# Revit family: 5863017284
name_source: partatom
category: Plumbing Fixtures
revit_build: Autodesk Revit 2018 (Build: 20170223_1515(x64)
units: mm (PartAtom-declared; Revit-internal decimal feet)

## family parameters
Always vertical = Yes
Cut with Voids When Loaded = No
OmniClass Number = 23.45.55.00
OmniClass Title = Sanitary Faucets, Wastes
Part Type = Normal
Room Calculation Point = No
Round Connector Dimension = Use Diameter
Shared = No
Work Plane-Based = No

## types (1)
- 5863017284 Shower faucet, 6 V, Bluetooth
    2D/3D/BIM Files URL = http://static.hansa.com
    3D View = https://static.hansa.com
    Additional Features = protected against back-flow in domestic use (according to DIN EN 1717)
    Advanced Features = Safety glass;Software settings adjustable via App
    Ambience photo = http://static.hansa.com
    AssetType = Fixed
    BIMObjectName = 5863017284
    Backflow Prevention EN1717 = EB
    Battery = AA 1.5 V Lithium x 4
    Bluetooth = 4.x
    BodyMaterial = Brass
    Brand = HANSA
    Catalog Drawing URL = http://static.hansa.com
    Category = Bathroom;Shower
    CloseOffRating = 0
    Color = 549
    Connection = Ball eccentric coupling(s)
    Connection Size = G1/2
    Dimension Drawing URL = http://static.hansa.com
    DurationUnit = Year
    EAN Number = 4057304008740
    EMC Directive = 2014/53/EU , 2011/65/EU
    EN Standard = EN 1111 , EN 15091
    ETIM Class Number = EC010340 Electronic tap
    Electronic Parts = Solenoid valve;Light indicated function(s);Low battery indicator
    FDV Document URL = http://www.hansa.com
    FaucetMainMaterial = Brass
    Features = Thermostatic;Bluetooth®;Battery-operated
    Finish = Polished
    Flow Drawing URL = http://static.hansa.com
    Flow Rate At 300kPa = 0.2 L/s
    FlowCoefficient = 0
    Group = Shower faucet
    IfcExportAs = IfcValveType
    IfcExportType = FAUCET
    Installation Type = Wall mounted
    Installation Width = CC150± 15 mm
    Installation and Maintenance Guide URL = http://static.hansa.com
    Interactive AR View URL = https://static.hansa.com
    Lever Handle = Temperature control handle;Flow control handle
    Manufacturer = HANSA
    ManufacturerName = HANSA
    ManufacturerURL = http://www.hansa.com
    Market = Austria;Belgium;Czech Republic;Germany;Spain;France;International;Italy;Netherlands;Slovakia
    Material = Brass
    Max. Hot Water Supply = 70 °C
    Mechanical Parts = Thermostatic cartridge for automatic temperature control
    Mobile Product Information URL = http://mpi.hansa.com
    Model = 5863017284 Shower faucet, 6 V, Bluetooth
    ModelReference = 5863017284
    NBSDescription = Shower mixers
    NBSReference = 45-35-70/335
    Name = 5863017284 Shower faucet, 6 V, Bluetooth
    Name_en = 5863017284 Shower faucet, 6 V, Bluetooth
    Noise Class = I (ISO 3822) Oras lab.
    NominalDepth = 146 mm
    NominalHeight = 78 mm  [stored 0.255906 ft]
    NominalWidth = 371 mm
    Operating Voltage = 6 V
    Pressure Loss With Flow 02ls = 300000.0 Pa
    Product Code = 5863017284
    Product Family = HANSAEMOTION Wellfit
    Product Image URL = http://static.hansa.com
    Product URL = http://static.hansa.com
    Protection Class = IP 55
    Revision = 3
    Sales Package dimensions (LxWxH) = 415 x 183 x 147
    Shape = Sculptured
    Size = 370x145x80 mm
    Spare-Part Information URL = http://static.hansa.com
    Surface treatment = Chrome/Grey
    Technical DataSheet URL = http://www.hansa.com
    Temperature = Thermostatic safety stop at 38°C;THERMO COOL
    Temperature Adjustments = Safety stop against scalding at 38°C;The housing of the fittings conducts minimal heat
    UNSPSC Class Number = 30181700 Faucets or taps
    URL Declaration of Conformity = http://static.hansa.com
    URL REACH = http://static.hansa.com
    URL UN38.3 = http://www.hansa.com
    URL WEEE = http://www.hansa.com
    Uniclass2 = Pr_40_30_96_81
    Uniclass2015Description = Shower thermostatic water supply sets
    Uniclass2015Reference = Pr_40_20_87_81
    Version = 3
    VersionDate = 01/07/2022
    Warranty Information URL = http://warranty.hansa.com
    WarrantyDescription = http://warranty.hansa.com
    WarrantyDurationUnit = Year
    Working Pressure = 100 - 1000 kPa

note: [stored X ft] marks values corroborated as IEEE doubles in the binary element streams (Revit-internal decimal feet)

## geometry (parser evidence)
native form markers: Sweep x6
no freeform markers — native parametric forms only
